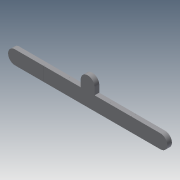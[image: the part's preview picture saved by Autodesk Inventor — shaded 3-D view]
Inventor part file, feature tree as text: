
AUTODESK INVENTOR PART (.ipt)
format: ipt  version: 2013 (Build 170138000, 138)  size: 169,984 bytes
history: native  units: mm
features: extrude x7, sketch x7
ambient origin geometry x8: Origin, YZ Plane, XZ Plane, XY Plane, X Axis, Y Axis, Z Axis, Center Point
bodies: Solid1 (feature_tree)
feature tree (14):
  extrude  "Extrusion1"  Depth=6.0mm
  extrude  "Extrusion2"  Depth=10.0mm
  extrude  "Extrusion3"  Depth=12.5mm
  extrude  "Extrusion4"  Depth=6.0mm
  extrude  "Extrusion5"  Depth=6.0mm
  extrude  "Extrusion6"  Depth=6.0mm
  extrude  "Extrusion7"  Depth=6.0mm
  sketch  "Sketch1"  dims[d0=18.0mm d1=6.0mm]
  sketch  "Sketch2"  dims[d2=10.0mm d3=10.0mm]
  sketch  "Sketch3"  dims[d4=12.5mm d5=12.5mm]
  sketch  "Sketch4"  dims[d6=6.0mm d7=6.0mm]
  sketch  "Sketch5"  dims[d8=0.01mm d9=6.0mm]
  sketch  "Sketch6"  dims[d10=0.01mm d11=6.0mm]
  sketch  "Sketch7"  dims[d12=0.01mm d13=6.0mm d14=0.01mm d15=6.0mm d16=0.01mm d17=0.01mm d18=2.0mm d19=0.0mm d20=3.0mm d21=3.0mm d22=3.0mm d23=1.5mm d24=3.0mm d25=3.0mm d26=2.0mm d27=0.0mm d28=0.01mm d29=0.01mm d30=2.0mm d31=0.0mm d32=0.01mm d33=2.0mm d34=0.0mm d35=0.1mm d36=0.1mm d37=2.0mm d38=0.0mm d39=0.1mm d40=2.0mm d41=0.0mm d42=0.1mm d43=2.0mm d44=0.0mm]
